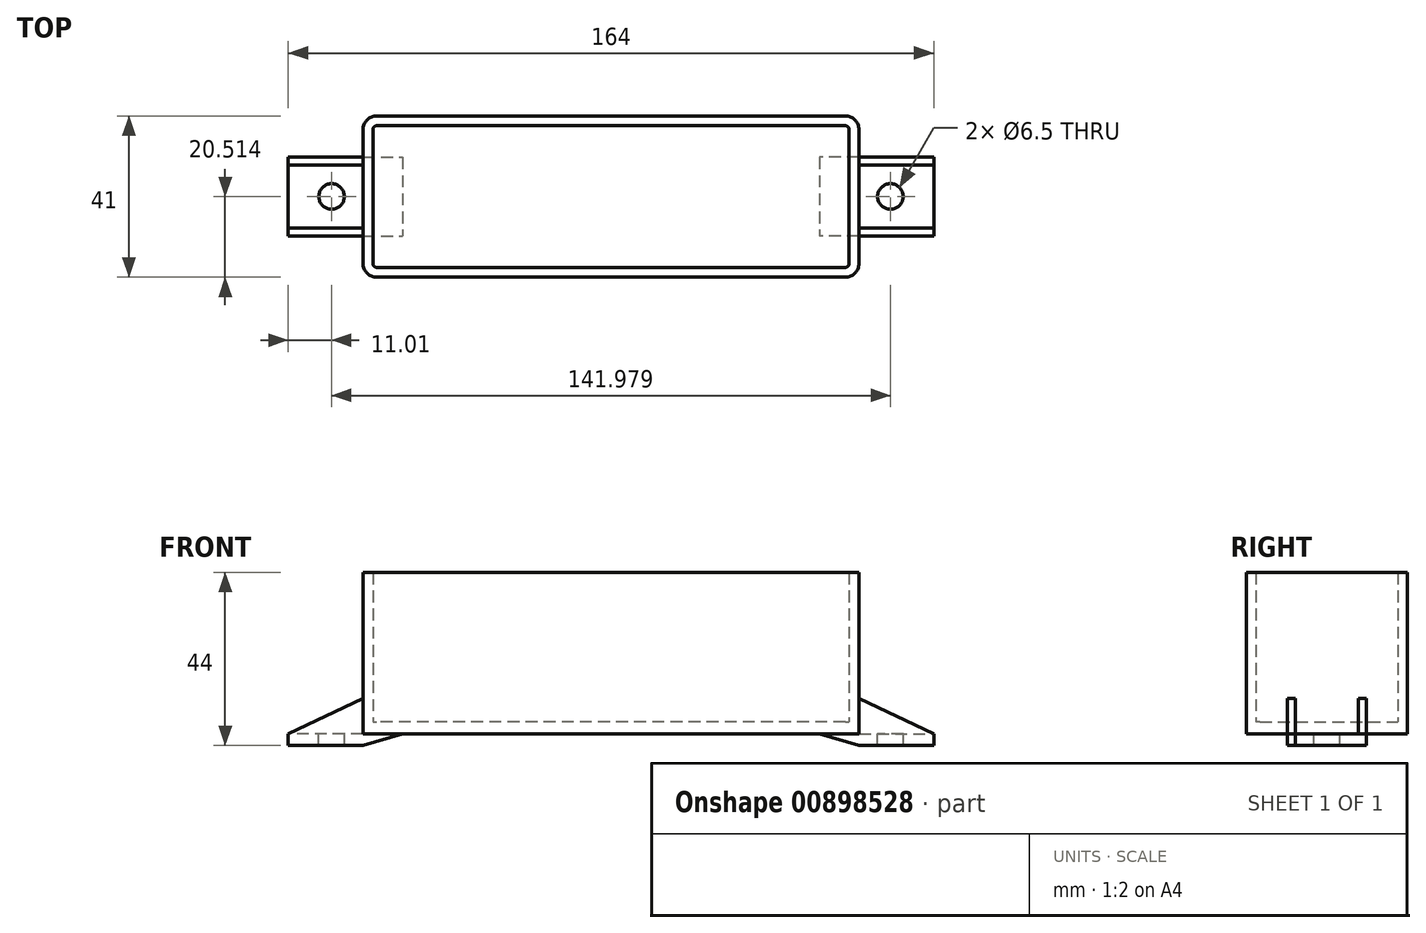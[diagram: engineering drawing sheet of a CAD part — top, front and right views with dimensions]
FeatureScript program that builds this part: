
annotation { "Feature Type Name" : "Feature", "Feature Type Description" : "" }
export const myFeature = defineFeature(function(context is Context, id is Id, definition is map)
    precondition{}
    {
        {
            var Q0;
            Q0=qCreatedBy(makeId("Top.planeOp"),FACE);
            var sketch = newSketch(context, id + "F0", { "sketchPlane" : qUnion([Q0])});
            skPoint(sketch, "E0.middle", {"position": v(0, 0) * mm});
            skPoint(sketch, "E1.visualSharp", {"position": v(-63, 20.5) * mm});
            skPoint(sketch, "E2.visualSharp", {"position": v(-63, -20.5) * mm});
            skPoint(sketch, "E3.visualSharp", {"position": v(63, -20.5) * mm});
            skPoint(sketch, "E4.visualSharp", {"position": v(63, 20.5) * mm});
            skPoint(sketch, "E5.visualSharp", {"position": v(-60.5, 18) * mm});
            skPoint(sketch, "E6.visualSharp", {"position": v(-60.5, -18) * mm});
            skPoint(sketch, "E7.visualSharp", {"position": v(60.5, -18) * mm});
            skPoint(sketch, "E8.visualSharp", {"position": v(60.5, 18) * mm});
            skLineSegment(sketch, "E9", {"start": v(-63, -20.5) * mm, "end": v(-63, 20.5) * mm});
            skLineSegment(sketch, "E10", {"start": v(-63, 20.5) * mm, "end": v(63, 20.5) * mm});
            skLineSegment(sketch, "E11", {"start": v(63, -20.5) * mm, "end": v(63, 20.5) * mm});
            skLineSegment(sketch, "E12", {"start": v(60.5, 18) * mm, "end": v(-60.5, 18) * mm});
            skLineSegment(sketch, "E13", {"start": v(-60.5, 18) * mm, "end": v(-60.5, -18) * mm});
            skLineSegment(sketch, "E14", {"start": v(-63, -20.5) * mm, "end": v(63, -20.5) * mm});
            skLineSegment(sketch, "E15", {"start": v(60.5, -18) * mm, "end": v(-60.5, -18) * mm});
            skLineSegment(sketch, "E16", {"start": v(60.5, -18) * mm, "end": v(60.5, 18) * mm});
            skSolve(sketch);
        }
        {
            var Q0;
            Q0=makeQuery(id+"F0.imprint","IMPRINT",FACE,{"disambiguationData":[TD([[makeQuery(id+"F0.imprint","IMPRINT",EDGE,{"derivedFrom":sQuery(id+"F0.wireOp",EDGE,"E9")}),-1.0]])]});
            extrude(context, id + "F1", {"entities" : qUnion([Q0]), "depth" : 41 * mm, "offsetDistance" : 25 * mm});
        }
        {
            var Q0;
            Q0=makeQuery(id+"F0.imprint","IMPRINT",FACE,{"disambiguationData":[TD([[makeQuery(id+"F0.imprint","IMPRINT",EDGE,{"derivedFrom":sQuery(id+"F0.wireOp",EDGE,"E12")}),1.0]])]});
            extrude(context, id + "F2", {"entities" : qUnion([Q0]), "operationType" : NewBodyOperationType.ADD, "depth" : 3 * mm, "offsetDistance" : 25 * mm});
        }
        {
            var Q0;
            Q0=qCreatedBy(makeId("Top.planeOp"),FACE);
            var sketch = newSketch(context, id + "F3", { "sketchPlane" : qUnion([Q0])});
            skLineSegment(sketch, "E17", {"start": v(0, 0) * mm, "end": v(0, -20.5) * mm});
            skLineSegment(sketch, "E18", {"start": v(0, -20.5) * mm, "end": v(0, 20.5) * mm});
            skLineSegment(sketch, "E19.MirrorCS", {"start": v(81.98, 8) * mm, "end": v(82, 8) * mm});
            skLineSegment(sketch, "E20.MirrorCS", {"start": v(82, 10) * mm, "end": v(82, 8) * mm});
            skLineSegment(sketch, "E21.MirrorCS", {"start": v(63, -10) * mm, "end": v(63, -8) * mm});
            skLineSegment(sketch, "E22.MirrorCS", {"start": v(63, 8) * mm, "end": v(63, 10) * mm});
            skLineSegment(sketch, "E23.MirrorCS", {"start": v(82, -10) * mm, "end": v(81.98, -8) * mm});
            skLineSegment(sketch, "E24.MirrorCS", {"start": v(63, 10) * mm, "end": v(53, 10) * mm});
            skLineSegment(sketch, "E25.MirrorCS", {"start": v(63, -8) * mm, "end": v(81.98, -8) * mm});
            skLineSegment(sketch, "E26.MirrorCS", {"start": v(63, 8) * mm, "end": v(63, -8) * mm});
            skLineSegment(sketch, "E27.MirrorCS", {"start": v(63, -10) * mm, "end": v(63, -10) * mm});
            skLineSegment(sketch, "E28.MirrorCS", {"start": v(82, -10) * mm, "end": v(63, -10) * mm});
            skLineSegment(sketch, "E29.MirrorCS", {"start": v(63, 8) * mm, "end": v(63, 8) * mm});
            skLineSegment(sketch, "E30.MirrorCS", {"start": v(53, -8) * mm, "end": v(63, -8) * mm});
            skLineSegment(sketch, "E31.MirrorCS", {"start": v(82, 10) * mm, "end": v(63, 10) * mm});
            skLineSegment(sketch, "E32.MirrorCS", {"start": v(53, 10) * mm, "end": v(53, -10) * mm});
            skLineSegment(sketch, "E33.MirrorCS", {"start": v(53, 8) * mm, "end": v(81.98, 8) * mm});
            skLineSegment(sketch, "E34.MirrorCS", {"start": v(63, -10) * mm, "end": v(53, -10) * mm});
            skLineSegment(sketch, "E35", {"start": v(82, 8) * mm, "end": v(81.98, -8) * mm});
            skLineSegment(sketch, "E36", {"start": v(81.99, 0) * mm, "end": v(70.99, 0.01) * mm});
            skCircle(sketch, "E37", {"center": v(70.99, 0.01) * mm, "radius": 3.25 * mm});
            skLineSegment(sketch, "E38.MirrorCS", {"start": v(-81.98, 8) * mm, "end": v(-82, 8) * mm});
            skLineSegment(sketch, "E39.MirrorCS", {"start": v(-82, 10) * mm, "end": v(-82, 8) * mm});
            skLineSegment(sketch, "E40.MirrorCS", {"start": v(-63, 8) * mm, "end": v(-63, 10) * mm});
            skLineSegment(sketch, "E41.MirrorCS", {"start": v(-63, -10) * mm, "end": v(-63, -8) * mm});
            skLineSegment(sketch, "E42.MirrorCS", {"start": v(-82, -10) * mm, "end": v(-81.98, -8) * mm});
            skLineSegment(sketch, "E43.MirrorCS", {"start": v(-82, 8) * mm, "end": v(-81.98, -8) * mm});
            skLineSegment(sketch, "E44.MirrorCS", {"start": v(-63, 10) * mm, "end": v(-53, 10) * mm});
            skCircle(sketch, "E45.MirrorC", {"center": v(-70.99, 0.01) * mm, "radius": 3.25 * mm});
            skLineSegment(sketch, "E46.MirrorCS", {"start": v(-63, 8) * mm, "end": v(-63, -8) * mm});
            skLineSegment(sketch, "E47.MirrorCS", {"start": v(-82, -10) * mm, "end": v(-63, -10) * mm});
            skLineSegment(sketch, "E48.MirrorCS", {"start": v(-63, -10) * mm, "end": v(-53, -10) * mm});
            skLineSegment(sketch, "E49.MirrorCS", {"start": v(-53, -8) * mm, "end": v(-63, -8) * mm});
            skLineSegment(sketch, "E50.MirrorCS", {"start": v(-81.99, 0) * mm, "end": v(-70.99, 0.01) * mm});
            skLineSegment(sketch, "E51.MirrorCS", {"start": v(-63, 8) * mm, "end": v(-63, 8) * mm});
            skLineSegment(sketch, "E52.MirrorCS", {"start": v(-63, -10) * mm, "end": v(-63, -10) * mm});
            skLineSegment(sketch, "E53.MirrorCS", {"start": v(-82, 10) * mm, "end": v(-63, 10) * mm});
            skLineSegment(sketch, "E54.MirrorCS", {"start": v(-53, 10) * mm, "end": v(-53, -10) * mm});
            skLineSegment(sketch, "E55.MirrorCS", {"start": v(-53, 8) * mm, "end": v(-81.98, 8) * mm});
            skLineSegment(sketch, "E56.MirrorCS", {"start": v(-63, -8) * mm, "end": v(-81.98, -8) * mm});
            skSolve(sketch);
        }
        {
            var Q0;
            {var subQ1=sQuery(id+"F3.wireOp",EDGE,"E38.MirrorCS");Q0=makeQuery(id+"F3.imprint","IMPRINT",FACE,{"disambiguationData":[TD([[makeQuery(id+"F3.imprint","IMPRINT",EDGE,{"derivedFrom":subQ1}),-1.0]])]});}
            var Q1;
            {var subQ0=sQuery(id+"F3.wireOp",EDGE,"E40.MirrorCS");Q1=makeQuery(id+"F3.imprint","IMPRINT",FACE,{"disambiguationData":[TD([[makeQuery(id+"F3.imprint","IMPRINT",EDGE,{"derivedFrom":subQ0}),-1.0]])]});}
            var Q2;
            {var subQ0=sQuery(id+"F3.wireOp",EDGE,"E46.MirrorCS");Q2=makeQuery(id+"F3.imprint","IMPRINT",FACE,{"disambiguationData":[TD([[makeQuery(id+"F3.imprint","IMPRINT",EDGE,{"derivedFrom":subQ0}),1.0]])]});}
            var Q3;
            Q3=makeQuery(id+"F3.imprint","IMPRINT",FACE,{"disambiguationData":[TD([[makeQuery(id+"F3.imprint","IMPRINT",EDGE,{"derivedFrom":sQuery(id+"F3.wireOp",EDGE,"E41.MirrorCS")}),1.0]])]});
            var Q4;
            Q4=makeQuery(id+"F3.imprint","IMPRINT",FACE,{"disambiguationData":[TD([[makeQuery(id+"F3.imprint","IMPRINT",EDGE,{"derivedFrom":sQuery(id+"F3.wireOp",EDGE,"E41.MirrorCS")}),-1.0]])]});
            var Q5;
            Q5=makeQuery(id+"F3.imprint","IMPRINT",FACE,{"disambiguationData":[TD([[makeQuery(id+"F3.imprint","IMPRINT",EDGE,{"derivedFrom":sQuery(id+"F3.wireOp",EDGE,"E21.MirrorCS")}),-1.0]])]});
            var Q6;
            Q6=makeQuery(id+"F3.imprint","IMPRINT",FACE,{"disambiguationData":[TD([[makeQuery(id+"F3.imprint","IMPRINT",EDGE,{"derivedFrom":sQuery(id+"F3.wireOp",EDGE,"E21.MirrorCS")}),1.0]])]});
            var Q7;
            {var subQ0=sQuery(id+"F3.wireOp",EDGE,"E26.MirrorCS");Q7=makeQuery(id+"F3.imprint","IMPRINT",FACE,{"disambiguationData":[TD([[makeQuery(id+"F3.imprint","IMPRINT",EDGE,{"derivedFrom":subQ0}),-1.0]])]});}
            var Q8;
            {var subQ0=sQuery(id+"F3.wireOp",EDGE,"E22.MirrorCS");Q8=makeQuery(id+"F3.imprint","IMPRINT",FACE,{"disambiguationData":[TD([[makeQuery(id+"F3.imprint","IMPRINT",EDGE,{"derivedFrom":subQ0}),1.0]])]});}
            var Q9;
            {var subQ1=sQuery(id+"F3.wireOp",EDGE,"E19.MirrorCS");Q9=makeQuery(id+"F3.imprint","IMPRINT",FACE,{"disambiguationData":[TD([[makeQuery(id+"F3.imprint","IMPRINT",EDGE,{"derivedFrom":subQ1}),1.0]])]});}
            extrude(context, id + "F4", {"entities" : qUnion([Q0, Q1, Q2, Q3, Q4, Q5, Q6, Q7, Q8, Q9]), "operationType" : NewBodyOperationType.ADD, "endBound" : BoundingType.SYMMETRIC, "oppositeDirection" : true, "depth" : 6 * mm, "offsetDistance" : 25 * mm});
        }
        {
            var Q0;
            {var subQ4=sQuery(id+"F3.wireOp",EDGE,"E19.MirrorCS");Q0=makeQuery(id+"F3.imprint","IMPRINT",FACE,{"disambiguationData":[TD([[makeQuery(id+"F3.imprint","IMPRINT",EDGE,{"derivedFrom":subQ4}),-1.0]])]});}
            var Q1;
            {var subQ1=sQuery(id+"F3.wireOp",EDGE,"E38.MirrorCS");Q1=makeQuery(id+"F3.imprint","IMPRINT",FACE,{"disambiguationData":[TD([[makeQuery(id+"F3.imprint","IMPRINT",EDGE,{"derivedFrom":subQ1}),1.0]])]});}
            extrude(context, id + "F5", {"entities" : qUnion([Q0, Q1]), "operationType" : NewBodyOperationType.ADD, "oppositeDirection" : true, "depth" : 3 * mm, "offsetDistance" : 25 * mm});
        }
        {
            var Q0;
            {var subQ0=sQuery(id+"F3.wireOp",EDGE,"E39.MirrorCS");var subQ1=sQuery(id+"F3.wireOp",EDGE,"E55.MirrorCS");var subQ2=sQuery(id+"F3.wireOp",EDGE,"E38.MirrorCS");var subQ3=sQuery(id+"F3.wireOp",EDGE,"E46.MirrorCS");var subQ4=sQuery(id+"F3.wireOp",EDGE,"E53.MirrorCS");var subQ5=sQuery(id+"F3.wireOp",EDGE,"E44.MirrorCS");Q0=makeQuery(id+"F4.boolean.opBoolean","SPLIT",FACE,{"disambiguationData":[TD([makeQuery(id+"F4.opExtrude","SWEPT_FACE",FACE,{"disambiguationData":[OSD([subQ0])]})])],"derivedFrom":makeQuery(id+"F4.opExtrude","CAP_FACE",FACE,{"disambiguationData":[OSD([subQ2,subQ0,sQuery(id+"F3.wireOp",EDGE,"E42.MirrorCS"),subQ3,sQuery(id+"F3.wireOp",EDGE,"E47.MirrorCS"),sQuery(id+"F3.wireOp",EDGE,"E48.MirrorCS"),subQ5,subQ4,sQuery(id+"F3.wireOp",EDGE,"E54.MirrorCS"),subQ1,sQuery(id+"F3.wireOp",EDGE,"E56.MirrorCS")])],"isStart":true})});}
            var Q1;
            {var subQ0=sQuery(id+"F3.wireOp",EDGE,"E48.MirrorCS");var subQ1=sQuery(id+"F3.wireOp",EDGE,"E47.MirrorCS");var subQ2=sQuery(id+"F3.wireOp",EDGE,"E42.MirrorCS");var subQ3=sQuery(id+"F3.wireOp",EDGE,"E46.MirrorCS");var subQ4=sQuery(id+"F3.wireOp",EDGE,"E56.MirrorCS");Q1=makeQuery(id+"F4.boolean.opBoolean","SPLIT",FACE,{"disambiguationData":[TD([makeQuery(id+"F4.opExtrude","SWEPT_FACE",FACE,{"disambiguationData":[OSD([subQ2])]})])],"derivedFrom":makeQuery(id+"F4.opExtrude","CAP_FACE",FACE,{"disambiguationData":[OSD([sQuery(id+"F3.wireOp",EDGE,"E38.MirrorCS"),sQuery(id+"F3.wireOp",EDGE,"E39.MirrorCS"),subQ2,subQ3,subQ1,subQ0,sQuery(id+"F3.wireOp",EDGE,"E44.MirrorCS"),sQuery(id+"F3.wireOp",EDGE,"E53.MirrorCS"),sQuery(id+"F3.wireOp",EDGE,"E54.MirrorCS"),sQuery(id+"F3.wireOp",EDGE,"E55.MirrorCS"),subQ4])],"isStart":true})});}
            var Q2;
            {var subQ0=sQuery(id+"F3.wireOp",EDGE,"E31.MirrorCS");var subQ1=sQuery(id+"F3.wireOp",EDGE,"E24.MirrorCS");var subQ2=sQuery(id+"F3.wireOp",EDGE,"E20.MirrorCS");var subQ3=sQuery(id+"F3.wireOp",EDGE,"E33.MirrorCS");var subQ4=sQuery(id+"F3.wireOp",EDGE,"E19.MirrorCS");var subQ5=sQuery(id+"F3.wireOp",EDGE,"E26.MirrorCS");Q2=makeQuery(id+"F4.boolean.opBoolean","SPLIT",FACE,{"disambiguationData":[TD([makeQuery(id+"F4.opExtrude","SWEPT_FACE",FACE,{"disambiguationData":[OSD([subQ2])]})])],"derivedFrom":makeQuery(id+"F4.opExtrude","CAP_FACE",FACE,{"disambiguationData":[OSD([subQ4,subQ2,sQuery(id+"F3.wireOp",EDGE,"E23.MirrorCS"),subQ1,sQuery(id+"F3.wireOp",EDGE,"E25.MirrorCS"),subQ5,sQuery(id+"F3.wireOp",EDGE,"E28.MirrorCS"),subQ0,sQuery(id+"F3.wireOp",EDGE,"E32.MirrorCS"),subQ3,sQuery(id+"F3.wireOp",EDGE,"E34.MirrorCS")])],"isStart":true})});}
            var Q3;
            {var subQ0=sQuery(id+"F3.wireOp",EDGE,"E26.MirrorCS");var subQ1=sQuery(id+"F3.wireOp",EDGE,"E25.MirrorCS");var subQ2=sQuery(id+"F3.wireOp",EDGE,"E23.MirrorCS");var subQ3=sQuery(id+"F3.wireOp",EDGE,"E34.MirrorCS");var subQ4=sQuery(id+"F3.wireOp",EDGE,"E28.MirrorCS");Q3=makeQuery(id+"F4.boolean.opBoolean","SPLIT",FACE,{"disambiguationData":[TD([makeQuery(id+"F4.opExtrude","SWEPT_FACE",FACE,{"disambiguationData":[OSD([subQ2])]})])],"derivedFrom":makeQuery(id+"F4.opExtrude","CAP_FACE",FACE,{"disambiguationData":[OSD([sQuery(id+"F3.wireOp",EDGE,"E19.MirrorCS"),sQuery(id+"F3.wireOp",EDGE,"E20.MirrorCS"),subQ2,sQuery(id+"F3.wireOp",EDGE,"E24.MirrorCS"),subQ1,subQ0,subQ4,sQuery(id+"F3.wireOp",EDGE,"E31.MirrorCS"),sQuery(id+"F3.wireOp",EDGE,"E32.MirrorCS"),sQuery(id+"F3.wireOp",EDGE,"E33.MirrorCS"),subQ3])],"isStart":true})});}
            extrude(context, id + "F6", {"entities" : qUnion([Q0, Q1, Q2, Q3]), "operationType" : NewBodyOperationType.ADD, "depth" : 6 * mm, "offsetDistance" : 25 * mm});
        }
        {
            var Q0;
            {var subQ0=sQuery(id+"F3.wireOp",EDGE,"E34.MirrorCS");var subQ1=sQuery(id+"F3.wireOp",EDGE,"E28.MirrorCS");Q0=makeQuery(id+"F6.boolean.opBoolean","MERGE",FACE,{"derivedFrom":[makeQuery(id+"F4.opExtrude","SWEPT_FACE",FACE,{"disambiguationData":[OSD([subQ1,subQ0])]}),makeQuery(id+"F6.opExtrude","SWEPT_FACE",FACE,{"disambiguationData":[OSD([subQ1,subQ0])]})]});}
            var sketch = newSketch(context, id + "F7", { "sketchPlane" : qUnion([Q0])});
            skLineSegment(sketch, "E57", {"start": v(-82, 0) * mm, "end": v(-82, -3) * mm});
            skLineSegment(sketch, "E58", {"start": v(-82, 0) * mm, "end": v(-63, 9) * mm});
            skLineSegment(sketch, "E59", {"start": v(0, -3) * mm, "end": v(0, -27.47) * mm});
            skLineSegment(sketch, "E60", {"start": v(-63, -3) * mm, "end": v(-53, 0) * mm});
            skLineSegment(sketch, "E61", {"start": v(-82, 9) * mm, "end": v(-63, 9) * mm});
            skLineSegment(sketch, "E62", {"start": v(-82, 0) * mm, "end": v(-82, 9) * mm});
            skLineSegment(sketch, "E63", {"start": v(-53, -3) * mm, "end": v(-53, 0) * mm});
            skLineSegment(sketch, "E64", {"start": v(-63, -3) * mm, "end": v(-53, -3) * mm});
            skLineSegment(sketch, "E65.MirrorCS", {"start": v(63, -3) * mm, "end": v(53, 0) * mm});
            skLineSegment(sketch, "E66.MirrorCS", {"start": v(63, -3) * mm, "end": v(53, -3) * mm});
            skLineSegment(sketch, "E67.MirrorCS", {"start": v(53, -3) * mm, "end": v(53, 0) * mm});
            skLineSegment(sketch, "E68.MirrorCS", {"start": v(82, 0) * mm, "end": v(63, 9) * mm});
            skLineSegment(sketch, "E69.MirrorCS", {"start": v(82, 0) * mm, "end": v(82, 9) * mm});
            skLineSegment(sketch, "E70.MirrorCS", {"start": v(82, 9) * mm, "end": v(63, 9) * mm});
            skSolve(sketch);
        }
        {
            var Q0;
            Q0=makeQuery(id+"F7.imprint","IMPRINT",FACE,{"disambiguationData":[TD([[makeQuery(id+"F7.imprint","IMPRINT",EDGE,{"derivedFrom":sQuery(id+"F7.wireOp",EDGE,"E68.MirrorCS")}),-1.0]])]});
            var Q1;
            Q1=makeQuery(id+"F7.imprint","IMPRINT",FACE,{"disambiguationData":[TD([[makeQuery(id+"F7.imprint","IMPRINT",EDGE,{"derivedFrom":sQuery(id+"F7.wireOp",EDGE,"E65.MirrorCS")}),1.0]])]});
            var Q2;
            Q2=makeQuery(id+"F7.imprint","IMPRINT",FACE,{"disambiguationData":[TD([[makeQuery(id+"F7.imprint","IMPRINT",EDGE,{"derivedFrom":sQuery(id+"F7.wireOp",EDGE,"E58")}),1.0]])]});
            var Q3;
            Q3=makeQuery(id+"F7.imprint","IMPRINT",FACE,{"disambiguationData":[TD([[makeQuery(id+"F7.imprint","IMPRINT",EDGE,{"derivedFrom":sQuery(id+"F7.wireOp",EDGE,"E60")}),-1.0]])]});
            extrude(context, id + "F8", {"entities" : qUnion([Q0, Q1, Q2, Q3]), "operationType" : NewBodyOperationType.REMOVE, "oppositeDirection" : true, "depth" : 20 * mm, "offsetDistance" : 25 * mm});
        }
        {
            var Q0;
            Q0=makeQuery(id+"F1.opExtrude","SWEPT_EDGE",EDGE,{"disambiguationData":[OSD([sQuery(id+"F0.wireOp",EDGE,"E9"),sQuery(id+"F0.wireOp",EDGE,"E14")])]});
            var Q1;
            Q1=makeQuery(id+"F1.opExtrude","SWEPT_EDGE",EDGE,{"disambiguationData":[OSD([sQuery(id+"F0.wireOp",EDGE,"E9"),sQuery(id+"F0.wireOp",EDGE,"E10")])]});
            var Q2;
            Q2=makeQuery(id+"F1.opExtrude","SWEPT_EDGE",EDGE,{"disambiguationData":[OSD([sQuery(id+"F0.wireOp",EDGE,"E10"),sQuery(id+"F0.wireOp",EDGE,"E11")])]});
            var Q3;
            Q3=makeQuery(id+"F1.opExtrude","SWEPT_EDGE",EDGE,{"disambiguationData":[OSD([sQuery(id+"F0.wireOp",EDGE,"E11"),sQuery(id+"F0.wireOp",EDGE,"E14")])]});
            fillet(context, id + "F9", {"entities" : qUnion([Q0, Q1, Q2, Q3]), "radius" : 3.5 * mm, "tangentPropagation" : true, "allowEdgeOverflow" : false});
        }
        {
            var Q0;
            Q0=makeQuery(id+"F2.opExtrude","CAP_EDGE",EDGE,{"disambiguationData":[OSD([sQuery(id+"F0.wireOp",EDGE,"E15")])],"isStart":false});
            var Q1;
            Q1=makeQuery(id+"F2.opExtrude","CAP_EDGE",EDGE,{"disambiguationData":[OSD([sQuery(id+"F0.wireOp",EDGE,"E16")])],"isStart":false});
            var Q2;
            Q2=makeQuery(id+"F1.opExtrude","SWEPT_EDGE",EDGE,{"disambiguationData":[OSD([sQuery(id+"F0.wireOp",EDGE,"E15"),sQuery(id+"F0.wireOp",EDGE,"E16")])]});
            var Q3;
            Q3=makeQuery(id+"F2.opExtrude","CAP_EDGE",EDGE,{"disambiguationData":[OSD([sQuery(id+"F0.wireOp",EDGE,"E12")])],"isStart":false});
            var Q4;
            Q4=makeQuery(id+"F1.opExtrude","SWEPT_EDGE",EDGE,{"disambiguationData":[OSD([sQuery(id+"F0.wireOp",EDGE,"E12"),sQuery(id+"F0.wireOp",EDGE,"E16")])]});
            var Q5;
            Q5=makeQuery(id+"F2.opExtrude","CAP_EDGE",EDGE,{"disambiguationData":[OSD([sQuery(id+"F0.wireOp",EDGE,"E13")])],"isStart":false});
            var Q6;
            Q6=makeQuery(id+"F1.opExtrude","SWEPT_EDGE",EDGE,{"disambiguationData":[OSD([sQuery(id+"F0.wireOp",EDGE,"E12"),sQuery(id+"F0.wireOp",EDGE,"E13")])]});
            var Q7;
            Q7=makeQuery(id+"F1.opExtrude","SWEPT_EDGE",EDGE,{"disambiguationData":[OSD([sQuery(id+"F0.wireOp",EDGE,"E13"),sQuery(id+"F0.wireOp",EDGE,"E15")])]});
            fillet(context, id + "F10", {"entities" : qUnion([Q0, Q1, Q2, Q3, Q4, Q5, Q6, Q7]), "radius" : 1 * mm, "tangentPropagation" : true, "allowEdgeOverflow" : false});
        }
    });
